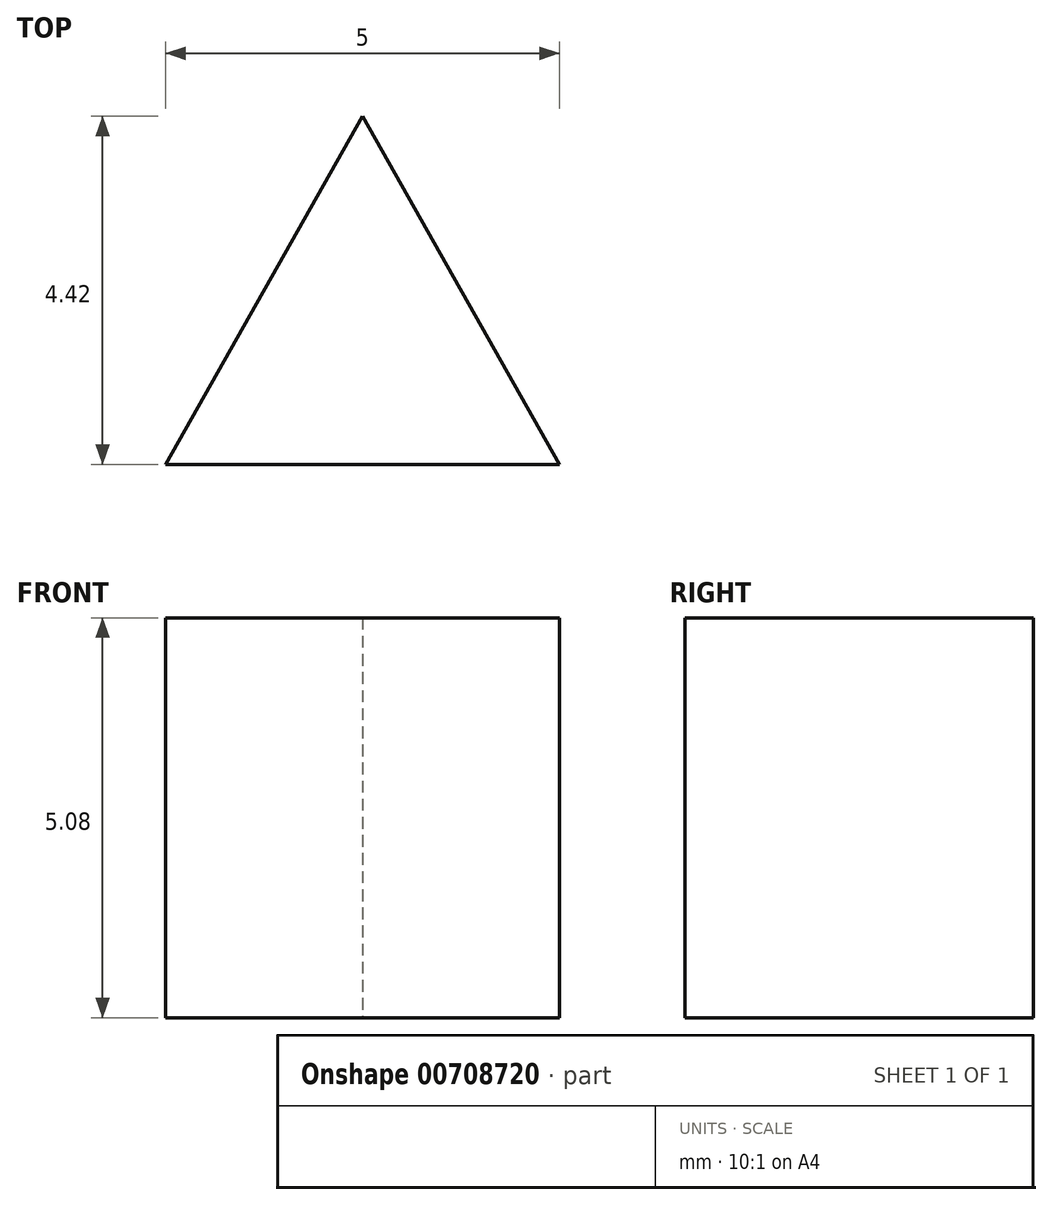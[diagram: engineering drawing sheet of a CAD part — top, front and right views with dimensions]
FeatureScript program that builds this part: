
annotation { "Feature Type Name" : "Feature", "Feature Type Description" : "" }
export const myFeature = defineFeature(function(context is Context, id is Id, definition is map)
    precondition{}
    {
        {
            var Q0;
            Q0=qCreatedBy(makeId("Top.planeOp"),FACE);
            var sketch = newSketch(context, id + "F0", { "sketchPlane" : qUnion([Q0])});
            skLineSegment(sketch, "E0", {"start": v(0, 0) * mm, "end": v(-2.5, -4.42) * mm});
            skLineSegment(sketch, "E1", {"start": v(-2.5, -4.42) * mm, "end": v(2.5, -4.42) * mm});
            skLineSegment(sketch, "E2", {"start": v(2.5, -4.42) * mm, "end": v(0, 0) * mm});
            skSolve(sketch);
        }
        {
            var Q0;
            Q0=makeQuery(id+"F0.imprint","IMPRINT",FACE,{"disambiguationData":[TD([[makeQuery(id+"F0.imprint","IMPRINT",EDGE,{"derivedFrom":sQuery(id+"F0.wireOp",EDGE,"E0")}),1.0]])]});
            extrude(context, id + "F1", {"entities" : qUnion([Q0]), "depth" : 5.08 * mm, "offsetDistance" : 25.4 * mm});
        }
    });
